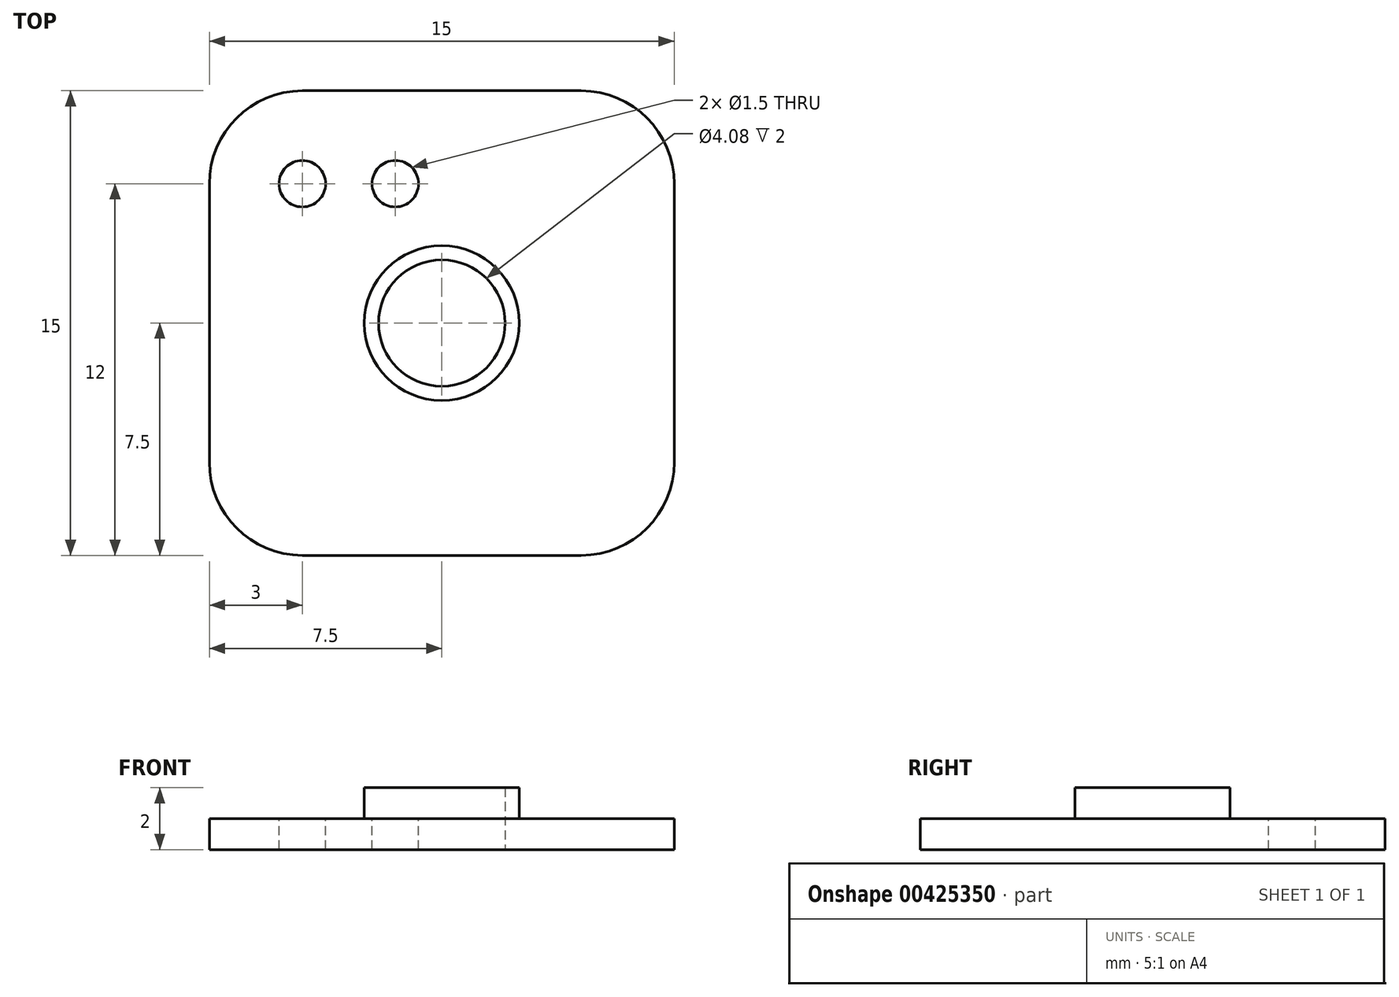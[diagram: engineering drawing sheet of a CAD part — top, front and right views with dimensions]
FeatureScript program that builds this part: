
annotation { "Feature Type Name" : "Feature", "Feature Type Description" : "" }
export const myFeature = defineFeature(function(context is Context, id is Id, definition is map)
    precondition{}
    {
        {
            var Q0;
            Q0=qCreatedBy(makeId("Top.planeOp"),FACE);
            var sketch = newSketch(context, id + "F0", { "sketchPlane" : qUnion([Q0])});
            skCircle(sketch, "E0", {"center": v(0, 0) * mm, "radius": 2.04 * mm});
            skCircle(sketch, "E1", {"center": v(0, 0) * mm, "radius": 2.5 * mm});
            skSolve(sketch);
        }
        {
            var Q0;
            Q0=makeQuery(id+"F0.imprint","IMPRINT",FACE,{"disambiguationData":[TD([[makeQuery(id+"F0.imprint","IMPRINT",EDGE,{"derivedFrom":sQuery(id+"F0.wireOp",EDGE,"E0")}),-1.0]])]});
            extrude(context, id + "F1", {"entities" : qUnion([Q0]), "depth" : 1 * mm});
        }
        {
            var Q0;
            Q0=makeQuery(id+"F1.opExtrude","CAP_FACE",FACE,{"disambiguationData":[OSD([sQuery(id+"F0.wireOp",EDGE,"E0"),sQuery(id+"F0.wireOp",EDGE,"E1")])],"isStart":true});
            var sketch = newSketch(context, id + "F2", { "sketchPlane" : qUnion([Q0])});
            skCircle(sketch, "E2", {"center": v(0, 0) * mm, "radius": 2.04 * mm});
            skCircle(sketch, "E3", {"center": v(0, 0) * mm, "radius": 5 * mm});
            skLineSegment(sketch, "E4.bottom", {"start": v(-7.5, -7.5) * mm, "end": v(7.5, -7.5) * mm});
            skLineSegment(sketch, "E4.top", {"start": v(-7.5, 7.5) * mm, "end": v(7.5, 7.5) * mm});
            skLineSegment(sketch, "E4.left", {"start": v(-7.5, -7.5) * mm, "end": v(-7.5, 7.5) * mm});
            skLineSegment(sketch, "E4.right", {"start": v(7.5, -7.5) * mm, "end": v(7.5, 7.5) * mm});
            skSolve(sketch);
        }
        {
            var Q0;
            Q0=makeQuery(id+"F2.imprint","IMPRINT",FACE,{"disambiguationData":[TD([[makeQuery(id+"F2.imprint","IMPRINT",EDGE,{"derivedFrom":sQuery(id+"F2.wireOp",EDGE,"E3")}),-1.0]])]});
            var Q1;
            Q1=makeQuery(id+"F2.imprint","IMPRINT",FACE,{"disambiguationData":[TD([[makeQuery(id+"F2.imprint","IMPRINT",EDGE,{"derivedFrom":sQuery(id+"F2.wireOp",EDGE,"E3")}),1.0]])]});
            var Q2;
            Q2=makeQuery(id+"F2.imprint","IMPRINT",FACE,{"disambiguationData":[TD([[makeQuery(id+"F2.imprint","IMPRINT",EDGE,{"derivedFrom":sQuery(id+"F2.wireOp",EDGE,"E2")}),1.0]])]});
            extrude(context, id + "F3", {"entities" : qUnion([Q0, Q1, Q2]), "operationType" : NewBodyOperationType.ADD, "depth" : 1 * mm});
        }
        {
            var Q0;
            Q0=makeQuery(id+"F3.opExtrude","SWEPT_EDGE",EDGE,{"disambiguationData":[OSD([sQuery(id+"F2.wireOp",EDGE,"E4.bottom"),sQuery(id+"F2.wireOp",EDGE,"E4.left")])]});
            var Q1;
            Q1=makeQuery(id+"F3.opExtrude","SWEPT_EDGE",EDGE,{"disambiguationData":[OSD([sQuery(id+"F2.wireOp",EDGE,"E4.bottom"),sQuery(id+"F2.wireOp",EDGE,"E4.right")])]});
            var Q2;
            Q2=makeQuery(id+"F3.opExtrude","SWEPT_EDGE",EDGE,{"disambiguationData":[OSD([sQuery(id+"F2.wireOp",EDGE,"E4.top"),sQuery(id+"F2.wireOp",EDGE,"E4.left")])]});
            var Q3;
            Q3=makeQuery(id+"F3.opExtrude","SWEPT_EDGE",EDGE,{"disambiguationData":[OSD([sQuery(id+"F2.wireOp",EDGE,"E4.top"),sQuery(id+"F2.wireOp",EDGE,"E4.right")])]});
            fillet(context, id + "F4", {"entities" : qUnion([Q0, Q1, Q2, Q3]), "radius" : 3 * mm, "tangentPropagation" : true, "allowEdgeOverflow" : false});
        }
        {
            var Q0;
            Q0=makeQuery(id+"F3.opExtrude","CAP_FACE",FACE,{"disambiguationData":[OSD([sQuery(id+"F2.wireOp",EDGE,"E2"),sQuery(id+"F2.wireOp",EDGE,"E4.bottom"),sQuery(id+"F2.wireOp",EDGE,"E4.top"),sQuery(id+"F2.wireOp",EDGE,"E4.left"),sQuery(id+"F2.wireOp",EDGE,"E4.right")])],"isStart":true});
            var sketch = newSketch(context, id + "F5", { "sketchPlane" : qUnion([Q0])});
            skCircle(sketch, "E5", {"center": v(-4.5, 4.5) * mm, "radius": 0.75 * mm});
            skCircle(sketch, "E6", {"center": v(-1.5, 4.5) * mm, "radius": 0.75 * mm});
            skSolve(sketch);
        }
        {
            var Q0;
            Q0 = qSketchRegion(id + "F5", true);
            extrude(context, id + "F6", {"entities" : qUnion([Q0]), "operationType" : NewBodyOperationType.REMOVE, "oppositeDirection" : true, "depth" : 25 * mm});
        }
    });
